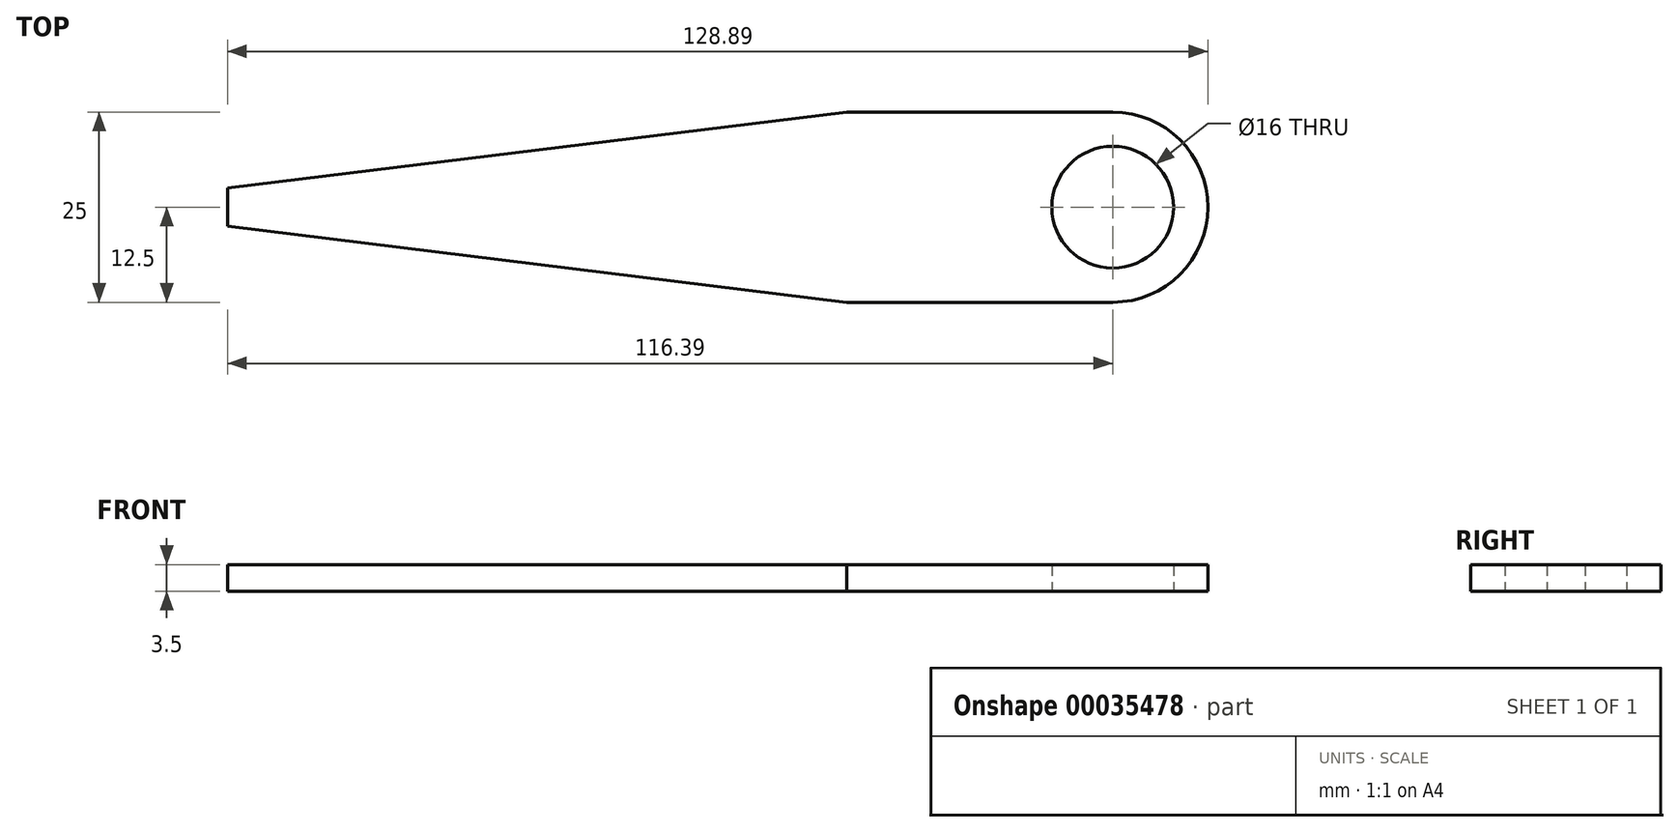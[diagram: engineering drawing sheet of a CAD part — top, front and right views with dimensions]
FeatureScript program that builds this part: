
annotation { "Feature Type Name" : "Feature", "Feature Type Description" : "" }
export const myFeature = defineFeature(function(context is Context, id is Id, definition is map)
    precondition{}
    {
        {
            var Q0;
            Q0=qCreatedBy(makeId("Top.planeOp"),FACE);
            var sketch = newSketch(context, id + "F0", { "sketchPlane" : qUnion([Q0])});
            skCircle(sketch, "E0", {"center": v(0, 0) * mm, "radius": 8 * mm});
            skCircle(sketch, "E1", {"center": v(0, 0) * mm, "radius": 12.5 * mm});
            skLineSegment(sketch, "E2", {"start": v(-35, 12.5) * mm, "end": v(0, 12.5) * mm});
            skLineSegment(sketch, "E3", {"start": v(-35, -12.5) * mm, "end": v(0, -12.5) * mm});
            skLineSegment(sketch, "E4", {"start": v(-35, 12.5) * mm, "end": v(-103.56, 12.5) * mm, "construction": true});
            skLineSegment(sketch, "E5", {"start": v(-35, 12.5) * mm, "end": v(-116.39, 2.5) * mm});
            skLineSegment(sketch, "E6", {"start": v(-35, -12.5) * mm, "end": v(-108.94, -12.5) * mm, "construction": true});
            skLineSegment(sketch, "E7", {"start": v(-35, -12.5) * mm, "end": v(-116.39, -2.5) * mm});
            skLineSegment(sketch, "E8", {"start": v(-116.39, 2.5) * mm, "end": v(-116.39, -2.5) * mm});
            skSolve(sketch);
        }
        {
            var Q0;
            {var subQ1=sQuery(id+"F0.wireOp",EDGE,"E2");Q0=makeQuery(id+"F0.imprint","IMPRINT",FACE,{"disambiguationData":[TD([[makeQuery(id+"F0.imprint","IMPRINT",EDGE,{"derivedFrom":subQ1}),-1.0]])]});}
            var Q1;
            Q1=makeQuery(id+"F0.imprint","IMPRINT",FACE,{"disambiguationData":[TD([[makeQuery(id+"F0.imprint","IMPRINT",EDGE,{"derivedFrom":sQuery(id+"F0.wireOp",EDGE,"E0")}),-1.0]])]});
            extrude(context, id + "F1", {"entities" : qUnion([Q0, Q1]), "depth" : 3.5 * mm});
        }
        {
            var Q0;
            Q0=makeQuery(id+"F1.opExtrude","CAP_FACE",FACE,{"disambiguationData":[OSD([sQuery(id+"F0.wireOp",EDGE,"E0"),sQuery(id+"F0.wireOp",EDGE,"E1"),sQuery(id+"F0.wireOp",EDGE,"E2"),sQuery(id+"F0.wireOp",EDGE,"E3"),sQuery(id+"F0.wireOp",EDGE,"E5"),sQuery(id+"F0.wireOp",EDGE,"E7"),sQuery(id+"F0.wireOp",EDGE,"E8")])],"isStart":false});
            var sketch = newSketch(context, id + "F2", { "sketchPlane" : qUnion([Q0])});
            skCircle(sketch, "E9", {"center": v(0, 0) * mm, "radius": 12.3 * mm});
            skSolve(sketch);
        }
        {
            var Q0;
            Q0=sQuery(id+"F2.wireOp",EDGE,"E9");
            extrude(context, id + "F3", {"bodyType" : ToolBodyType.SURFACE, "surfaceEntities" : qUnion([Q0]), "depth" : 1 * mm});
        }
    });
